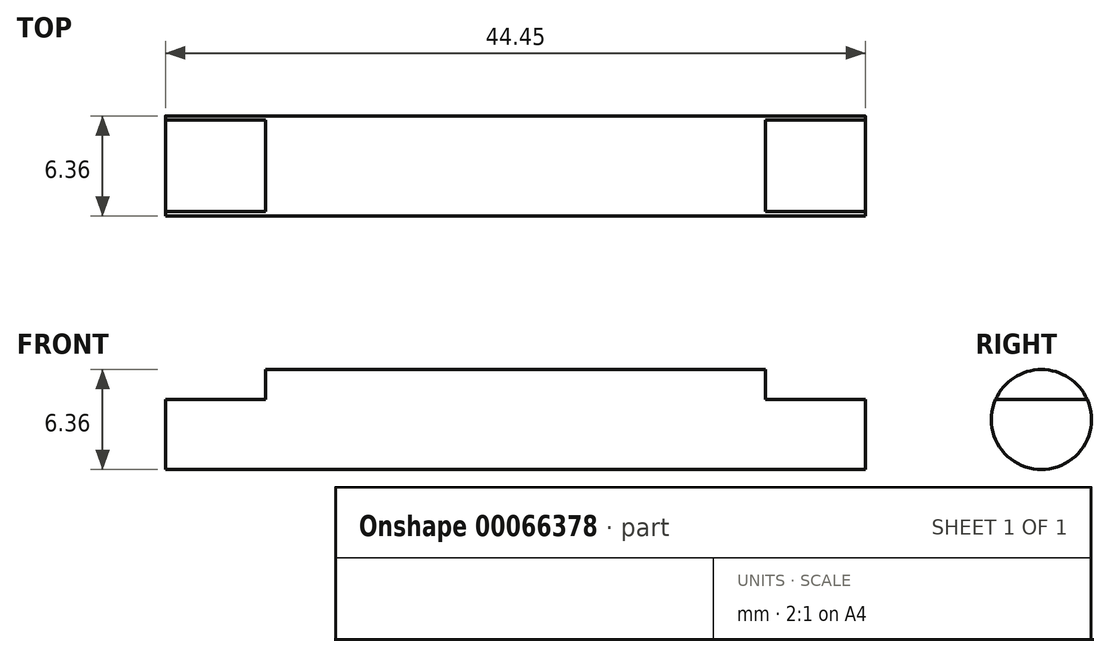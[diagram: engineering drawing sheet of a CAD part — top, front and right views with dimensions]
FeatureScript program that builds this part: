
annotation { "Feature Type Name" : "Feature", "Feature Type Description" : "" }
export const myFeature = defineFeature(function(context is Context, id is Id, definition is map)
    precondition{}
    {
        {
            var Q0;
            Q0=qCreatedBy(makeId("Right.planeOp"),FACE);
            var sketch = newSketch(context, id + "F0", { "sketchPlane" : qUnion([Q0])});
            skCircle(sketch, "E0", {"center": v(0, 0) * mm, "radius": 3.18 * mm});
            skSolve(sketch);
        }
        {
            var Q0;
            Q0 = qSketchRegion(id + "F0", true);
            extrude(context, id + "F1", {"entities" : qUnion([Q0]), "depth" : 44.45 * mm});
        }
        {
            var Q0;
            Q0=makeQuery(id+"F1.opExtrude","CAP_FACE",FACE,{"disambiguationData":[OSD([sQuery(id+"F0.wireOp",EDGE,"E0")])],"isStart":false});
            var sketch = newSketch(context, id + "F2", { "sketchPlane" : qUnion([Q0])});
            skLineSegment(sketch, "E1", {"start": v(-2.9, 1.27) * mm, "end": v(2.9, 1.27) * mm});
            skArc(sketch, "E2", {"start": v(2.9, 1.27) * mm, "mid": v(0, 3.18) * mm, "end": v(-2.9, 1.27) * mm});
            skSolve(sketch);
        }
        {
            var Q0;
            Q0 = qSketchRegion(id + "F2", true);
            extrude(context, id + "F3", {"entities" : qUnion([Q0]), "operationType" : NewBodyOperationType.REMOVE, "oppositeDirection" : true, "depth" : 6.35 * mm});
        }
        {
            var Q0;
            Q0=makeQuery(id+"F1.opExtrude","CAP_FACE",FACE,{"disambiguationData":[OSD([sQuery(id+"F0.wireOp",EDGE,"E0")])],"isStart":true});
            var sketch = newSketch(context, id + "F4", { "sketchPlane" : qUnion([Q0])});
            skArc(sketch, "E3", {"start": v(2.9, 1.27) * mm, "mid": v(0, 3.18) * mm, "end": v(-2.9, 1.27) * mm});
            skLineSegment(sketch, "E4", {"start": v(-2.9, 1.27) * mm, "end": v(2.9, 1.27) * mm});
            skSolve(sketch);
        }
        {
            var Q0;
            Q0 = qSketchRegion(id + "F4", true);
            extrude(context, id + "F5", {"entities" : qUnion([Q0]), "operationType" : NewBodyOperationType.REMOVE, "oppositeDirection" : true, "depth" : 6.35 * mm});
        }
    });
